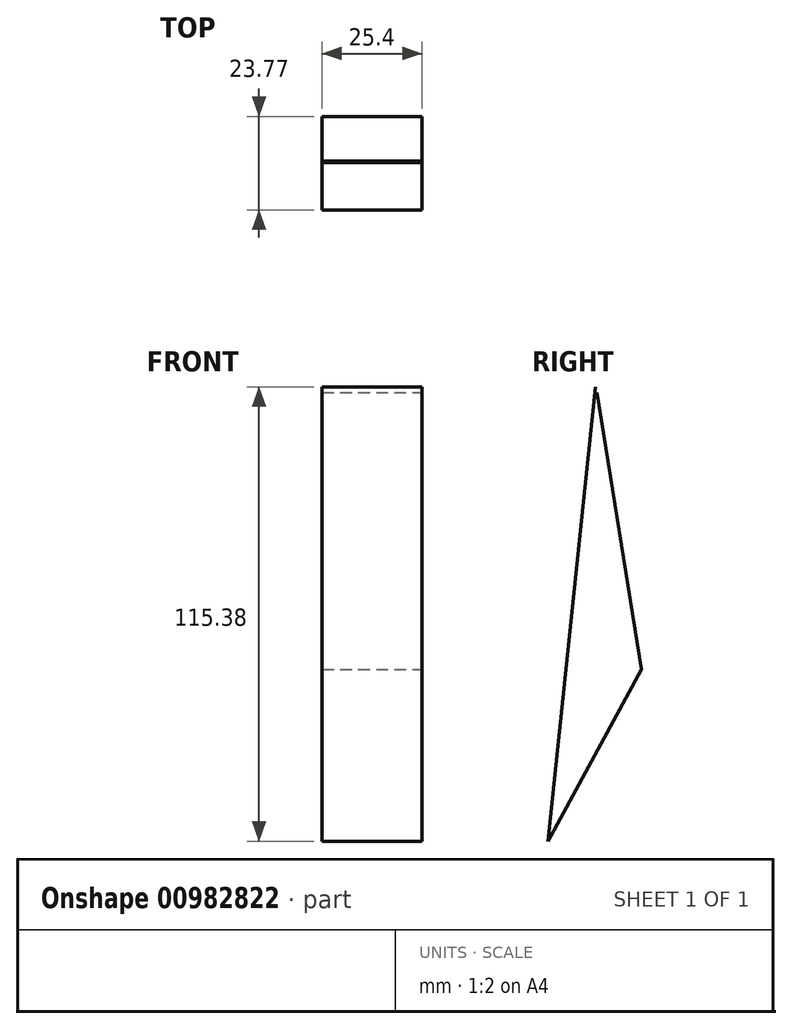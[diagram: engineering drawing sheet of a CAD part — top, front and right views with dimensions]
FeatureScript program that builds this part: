
annotation { "Feature Type Name" : "Feature", "Feature Type Description" : "" }
export const myFeature = defineFeature(function(context is Context, id is Id, definition is map)
    precondition{}
    {
        {
            var Q0;
            Q0=qCreatedBy(makeId("Right.planeOp"),FACE);
            var sketch = newSketch(context, id + "F0", { "sketchPlane" : qUnion([Q0])});
            skLineSegment(sketch, "E0", {"start": v(-63.03, -43.68) * mm, "end": v(-39.26, 0) * mm});
            skLineSegment(sketch, "E1", {"start": v(-39.26, 0) * mm, "end": v(-50.62, 70.25) * mm});
            skLineSegment(sketch, "E2", {"start": v(-50.97, 71.7) * mm, "end": v(-63.03, -43.68) * mm});
            skSolve(sketch);
        }
        {
            var Q0;
            Q0=sQuery(id+"F0.wireOp",EDGE,"E2");
            var Q1;
            Q1=sQuery(id+"F0.wireOp",EDGE,"E0");
            var Q2;
            Q2=sQuery(id+"F0.wireOp",EDGE,"E1");
            extrude(context, id + "F1", {"bodyType" : ToolBodyType.SURFACE, "surfaceEntities" : qUnion([Q0, Q1, Q2]), "depth" : 25.4 * mm, "offsetDistance" : 25.4 * mm});
        }
    });
